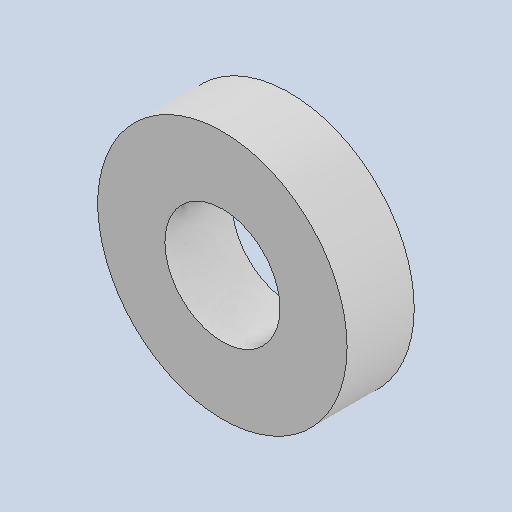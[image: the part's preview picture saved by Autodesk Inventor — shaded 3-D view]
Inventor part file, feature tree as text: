
AUTODESK INVENTOR PART (.ipt)
format: ipt  version: 2023 (Build 270158000, 158)  size: 218,624 bytes
history: native  units: in
note: dims shown in document units (in); Inventor stores cm internally (conversion verified against a paired STEP export)
features: extrude x1, sketch x1
ambient origin geometry x8: Origin, YZ Plane, XZ Plane, XY Plane, X Axis, Y Axis, Z Axis, Center Point
bodies: Solid1 (feature_tree)
feature tree (2):
  extrude  "Extrusion1"  Depth=0.4375in
  sketch  "Sketch1"  dims[d0=0.75in d1=1.625in d2=0.4375in d3=0.0in]
